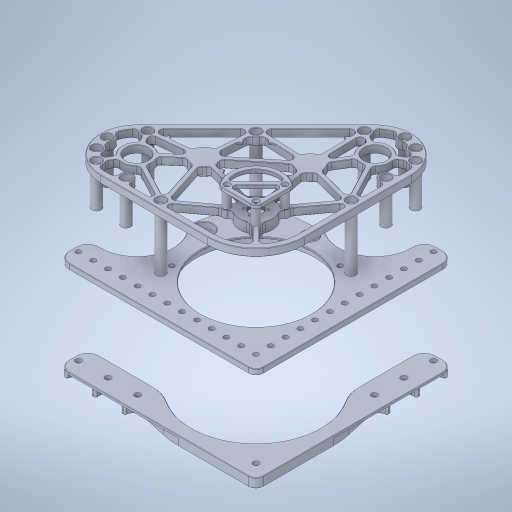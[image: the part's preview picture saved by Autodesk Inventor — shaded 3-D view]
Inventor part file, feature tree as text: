
AUTODESK INVENTOR PART (.ipt)
format: ipt  version: 2023.3 (Build 273359000, 359)  size: 1,731,072 bytes
history: native  units: in
note: dims shown in document units (in); Inventor stores cm internally (conversion verified against a paired STEP export)
features: other x14, chamfer x4, direct_edit x1, move_body x1
ambient origin geometry x8: Origin, YZ Plane, XZ Plane, XY Plane, X Axis, Y Axis, Z Axis, Center Point
bodies: Solid1 (feature_tree), Solid2 (feature_tree), Solid3 (feature_tree), Solid4 (feature_tree), Solid5 (feature_tree), Solid6 (feature_tree), Solid7 (feature_tree), Solid8 (feature_tree), Solid9 (feature_tree), Solid10 (feature_tree), Solid11 (feature_tree), Solid13 (feature_tree), Solid14 (feature_tree), Solid15 (feature_tree), Solid16 (feature_tree), Solid17 (feature_tree), Solid18 (feature_tree), Solid19 (feature_tree)
feature tree (20):
  direct_edit  "Direct Edit1"
  other  "Boss-Extrude4[1]"
  other  "Boss-Extrude4[2]"
  other  "Boss-Extrude4[3]"
  other  "Boss-Extrude6[1]"
  other  "Boss-Extrude6[2]"
  other  "Boss-Extrude6[3]"
  other  "Boss-Extrude6[4]"
  other  "Boss-Extrude6[5]"
  other  "Boss-Extrude6[6]"
  other  "Boss-Extrude6[7]"
  other  "Boss-Extrude6[8]"
  other  "Boss-Extrude17[1]"
  other  "Boss-Extrude17[2]"
  other  "Boss-Extrude17[3]"
  chamfer  "Chamfer4"  [1 undecoded]
  chamfer  "Chamfer1"  [1 undecoded]
  chamfer  "Chamfer3"  [1 undecoded]
  chamfer  "Chamfer2"  [1 undecoded]
  move_body  "Move1"
note: 4 required parameter values undecoded (feature->parameter linkage not recoverable at this tier; creation-order binding heuristic only, values carry confidence <= 0.55)
